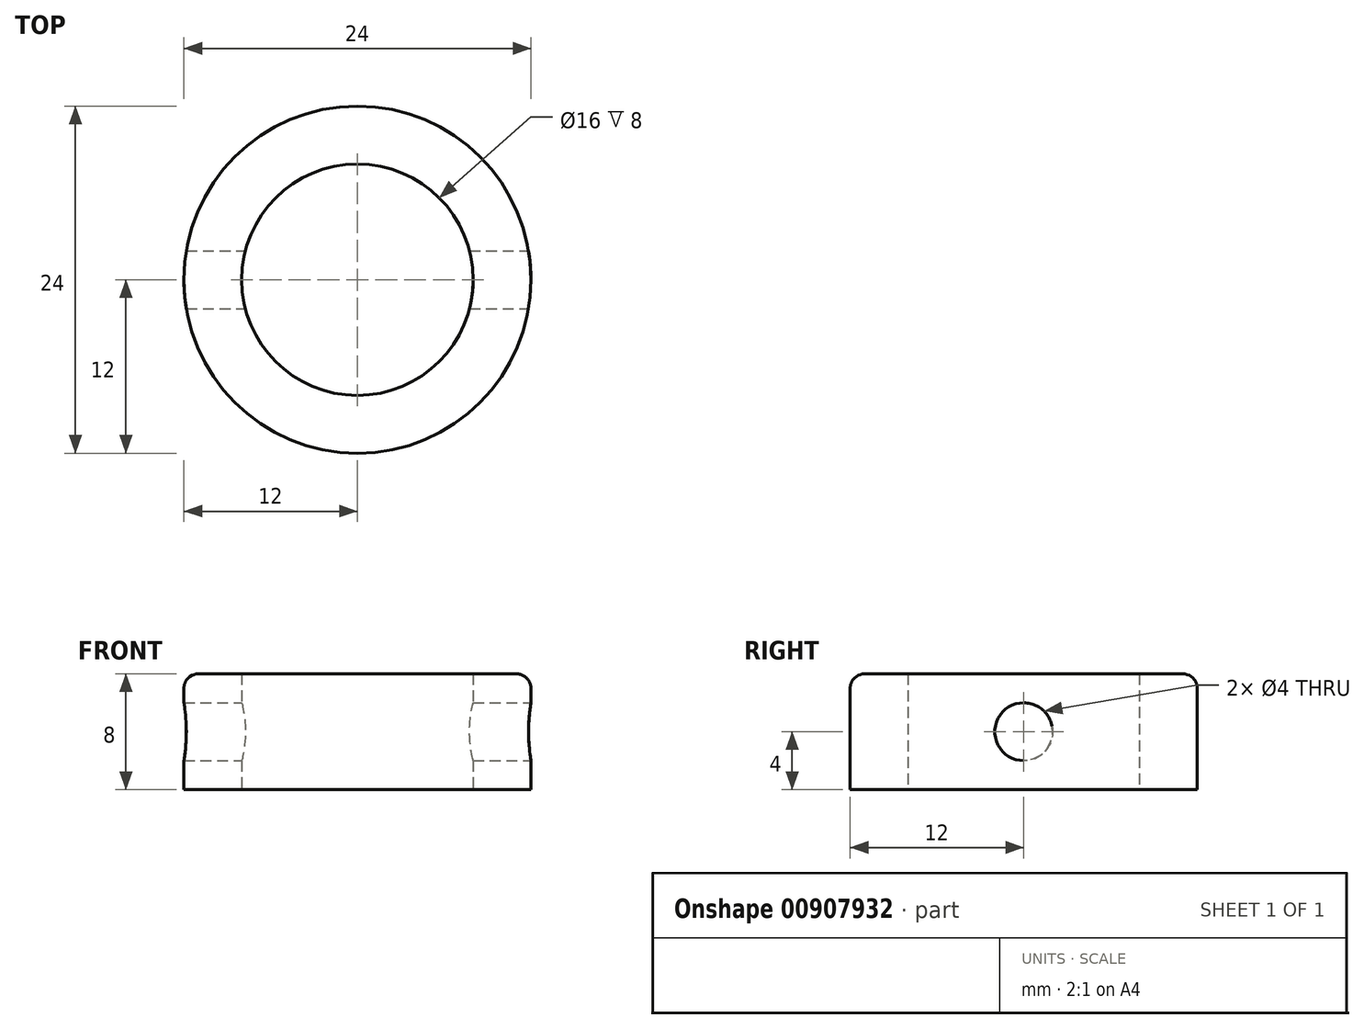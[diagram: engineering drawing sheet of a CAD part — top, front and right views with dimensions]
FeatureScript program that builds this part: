
annotation { "Feature Type Name" : "Feature", "Feature Type Description" : "" }
export const myFeature = defineFeature(function(context is Context, id is Id, definition is map)
    precondition{}
    {
        {
            var Q0;
            Q0=qCreatedBy(makeId("Top.planeOp"),FACE);
            var sketch = newSketch(context, id + "F0", { "sketchPlane" : qUnion([Q0])});
            skCircle(sketch, "E0", {"center": v(0, 0) * mm, "radius": 12 * mm});
            skCircle(sketch, "E1", {"center": v(0, 0) * mm, "radius": 8 * mm});
            skSolve(sketch);
        }
        {
            var Q0;
            Q0 = qSketchRegion(id + "F0", true);
            extrude(context, id + "F1", {"entities" : qUnion([Q0]), "depth" : 8 * mm, "offsetDistance" : 25 * mm});
        }
        {
            var Q0;
            Q0=makeQuery(id+"F1.opExtrude","CAP_EDGE",EDGE,{"disambiguationData":[OSD([sQuery(id+"F0.wireOp",EDGE,"E0")])],"isStart":false});
            fillet(context, id + "F2", {"entities" : qUnion([Q0]), "radius" : 1 * mm, "tangentPropagation" : true, "allowEdgeOverflow" : false});
        }
        {
            var Q0;
            Q0=qCreatedBy(makeId("Right.planeOp"),FACE);
            var sketch = newSketch(context, id + "F3", { "sketchPlane" : qUnion([Q0])});
            skCircle(sketch, "E2", {"center": v(0, 4) * mm, "radius": 2 * mm});
            skSolve(sketch);
        }
        {
            var Q0;
            Q0 = qSketchRegion(id + "F3", true);
            extrude(context, id + "F4", {"entities" : qUnion([Q0]), "operationType" : NewBodyOperationType.REMOVE, "endBound" : BoundingType.SYMMETRIC, "oppositeDirection" : true, "depth" : 60 * mm, "offsetDistance" : 25 * mm});
        }
    });
